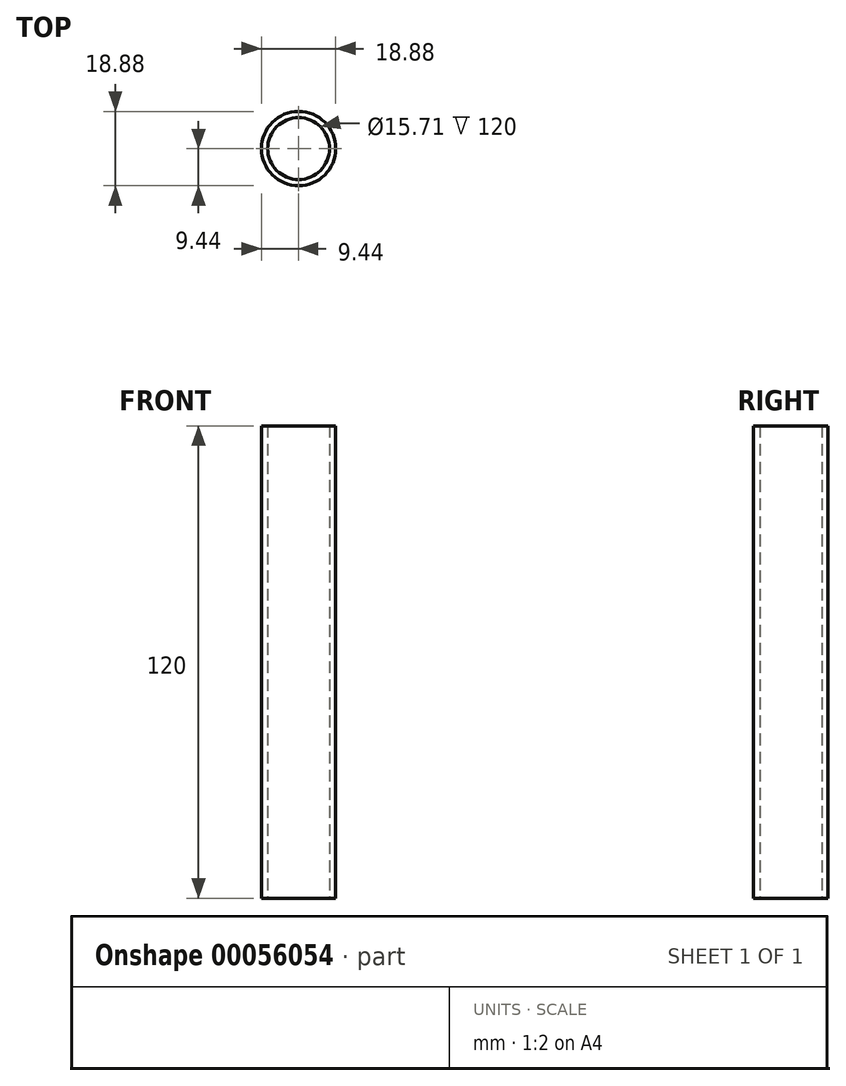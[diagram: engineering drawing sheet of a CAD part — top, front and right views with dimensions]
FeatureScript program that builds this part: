
annotation { "Feature Type Name" : "Feature", "Feature Type Description" : "" }
export const myFeature = defineFeature(function(context is Context, id is Id, definition is map)
    precondition{}
    {
        {
            var Q0;
            Q0=qCreatedBy(makeId("Top.planeOp"),FACE);
            var sketch = newSketch(context, id + "F0", { "sketchPlane" : qUnion([Q0])});
            skCircle(sketch, "E0", {"center": v(0, 0) * mm, "radius": 7.85 * mm});
            skCircle(sketch, "E1", {"center": v(0, 0) * mm, "radius": 9.44 * mm});
            skSolve(sketch);
        }
        {
            var Q0;
            Q0=makeQuery(id+"F0.imprint","IMPRINT",FACE,{"disambiguationData":[TD([[makeQuery(id+"F0.imprint","IMPRINT",EDGE,{"derivedFrom":sQuery(id+"F0.wireOp",EDGE,"E0")}),-1.0]])]});
            extrude(context, id + "F1", {"entities" : qUnion([Q0]), "depth" : 120 * mm});
        }
    });
